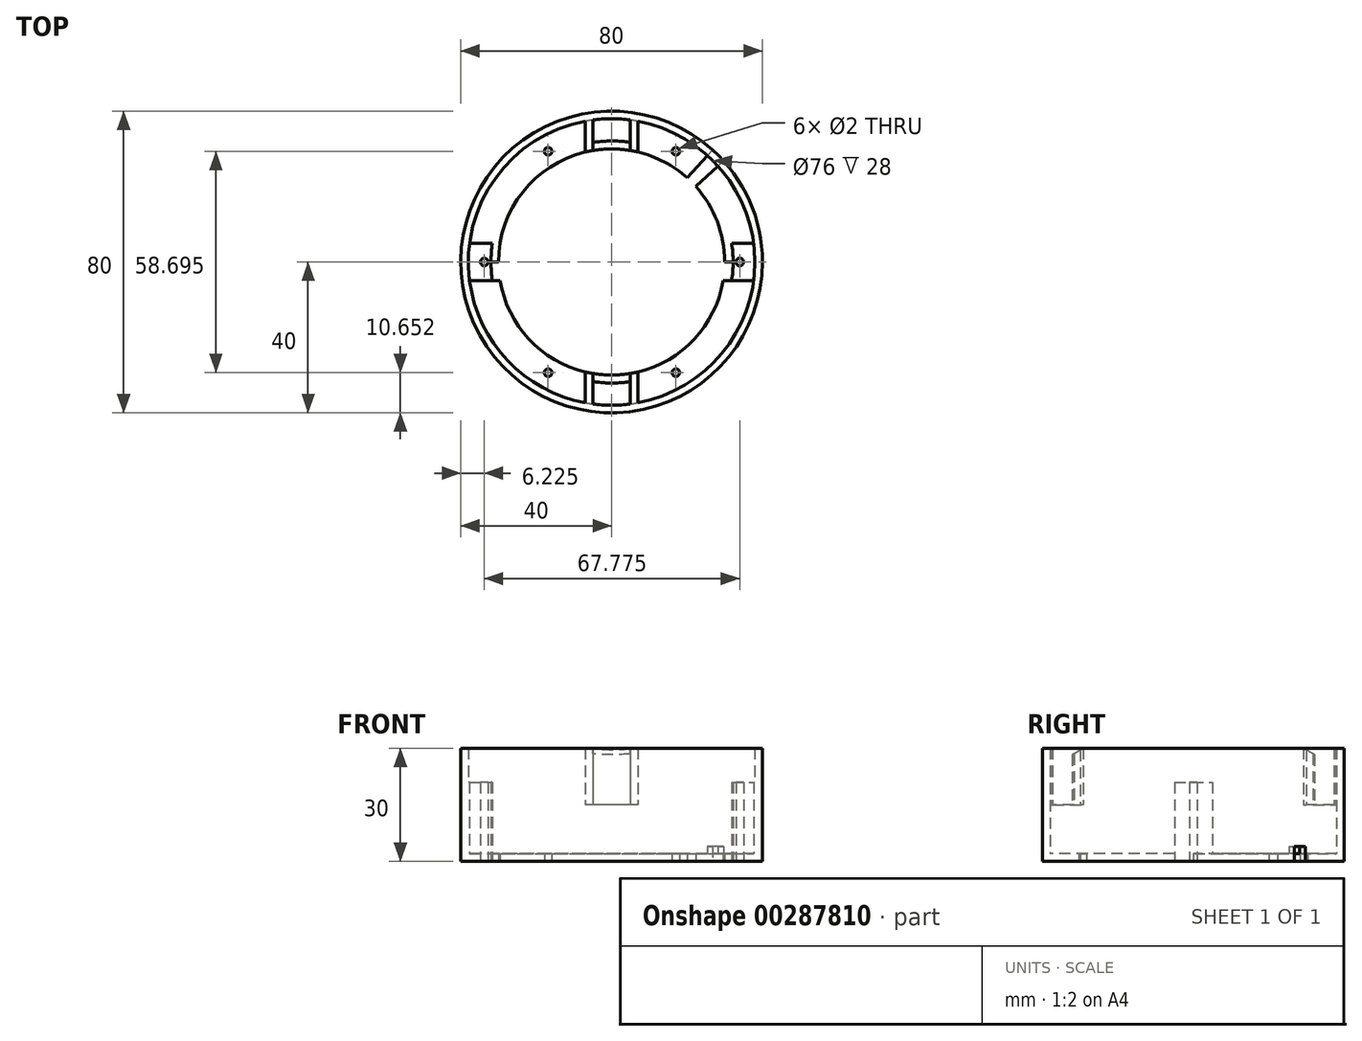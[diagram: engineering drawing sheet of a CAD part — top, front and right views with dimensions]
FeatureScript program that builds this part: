
annotation { "Feature Type Name" : "Feature", "Feature Type Description" : "" }
export const myFeature = defineFeature(function(context is Context, id is Id, definition is map)
    precondition{}
    {
        {
            var Q0;
            Q0=qCreatedBy(makeId("Top.planeOp"),FACE);
            var sketch = newSketch(context, id + "F0", { "sketchPlane" : qUnion([Q0])});
            skCircle(sketch, "E0", {"center": v(0, 0) * mm, "radius": 38 * mm});
            skCircle(sketch, "E1", {"center": v(0, 0) * mm, "radius": 40 * mm});
            skCircle(sketch, "E2", {"center": v(0, 0) * mm, "radius": 30 * mm});
            skLineSegment(sketch, "E3", {"start": v(-40, 0) * mm, "end": v(40, 0) * mm});
            skLineSegment(sketch, "E4", {"start": v(-39.69, 5) * mm, "end": v(39.69, 5) * mm});
            skLineSegment(sketch, "E5.MirrorCS", {"start": v(-39.69, -5) * mm, "end": v(39.69, -5) * mm});
            skCircle(sketch, "E6", {"center": v(34, 0) * mm, "radius": 1 * mm});
            skLineSegment(sketch, "E7", {"start": v(0, 40) * mm, "end": v(0, -40) * mm});
            skCircle(sketch, "E8.1.0", {"center": v(17.06, -29.35) * mm, "radius": 1 * mm});
            skCircle(sketch, "E8.2.0", {"center": v(-16.83, -29.35) * mm, "radius": 1 * mm});
            skCircle(sketch, "E8.3.0", {"center": v(-33.78, 0) * mm, "radius": 1 * mm});
            skCircle(sketch, "E8.4.0", {"center": v(-16.83, 29.35) * mm, "radius": 1 * mm});
            skCircle(sketch, "E8.5.0", {"center": v(17.06, 29.35) * mm, "radius": 1 * mm});
            skPoint(sketch, "E8.center", {"position": v(0.11, 0) * mm});
            skLineSegment(sketch, "E8.anchor1", {"start": v(0.11, 0) * mm, "end": v(34, 0) * mm, "construction": true});
            skLineSegment(sketch, "E8.anchor2", {"start": v(0.11, 0) * mm, "end": v(17.06, 29.35) * mm, "construction": true});
            skLineSegment(sketch, "E9", {"start": v(5, 29.58) * mm, "end": v(5, 37.67) * mm});
            skLineSegment(sketch, "E10", {"start": v(7, 37.35) * mm, "end": v(7, 29.17) * mm});
            skLineSegment(sketch, "E11.MirrorCS", {"start": v(-7, 37.35) * mm, "end": v(-7, 29.17) * mm});
            skLineSegment(sketch, "E12.MirrorCS", {"start": v(-5, 29.58) * mm, "end": v(-5, 37.67) * mm});
            skLineSegment(sketch, "E13.MirrorCS", {"start": v(-7, -37.35) * mm, "end": v(-7, -29.17) * mm});
            skLineSegment(sketch, "E14.MirrorCS", {"start": v(-5, -29.58) * mm, "end": v(-5, -37.67) * mm});
            skLineSegment(sketch, "E15.MirrorCS", {"start": v(5, -29.58) * mm, "end": v(5, -37.67) * mm});
            skLineSegment(sketch, "E16.MirrorCS", {"start": v(7, -37.35) * mm, "end": v(7, -29.17) * mm});
            skCircle(sketch, "E17", {"center": v(0.11, 0) * mm, "radius": 32.11 * mm});
            skLineSegment(sketch, "E18", {"start": v(0, 0) * mm, "end": v(28.28, 28.28) * mm});
            skLineSegment(sketch, "E19", {"start": v(0, 0) * mm, "end": v(29.73, 26.77) * mm});
            skLineSegment(sketch, "E20.MirrorCS", {"start": v(0, 0) * mm, "end": v(26.77, 29.73) * mm});
            skLineSegment(sketch, "E21", {"start": v(-12, 36.06) * mm, "end": v(-12, 27.5) * mm});
            skLineSegment(sketch, "E22.MirrorCS", {"start": v(12, 36.06) * mm, "end": v(12, 27.5) * mm});
            skLineSegment(sketch, "E23.MirrorCS", {"start": v(-12, -36.06) * mm, "end": v(-12, -27.5) * mm});
            skLineSegment(sketch, "E24.MirrorCS", {"start": v(12, -36.06) * mm, "end": v(12, -27.5) * mm});
            skSolve(sketch);
        }
        {
            var Q0;
            {var subQ0=sQuery(id+"F0.wireOp",EDGE,"E7");var subQ1=sQuery(id+"F0.wireOp",EDGE,"E0");var subQ2=makeQuery(id+"F0.imprint","INTERSECT",VERTEX,{"disambiguationData":[OD(0.0)],"derivedFrom":[subQ1,subQ0]});Q0=makeQuery(id+"F0.imprint","IMPRINT",FACE,{"disambiguationData":[TD([[makeQuery(id+"F0.imprint","IMPRINT",EDGE,{"disambiguationData":[TD([[subQ2,-1.0]])],"derivedFrom":subQ1}),-1.0]])]});}
            var Q1;
            {var subQ0=sQuery(id+"F0.wireOp",EDGE,"E4");var subQ1=sQuery(id+"F0.wireOp",EDGE,"E0");var subQ2=makeQuery(id+"F0.imprint","INTERSECT",VERTEX,{"disambiguationData":[OD(1.0)],"derivedFrom":[subQ1,subQ0]});Q1=makeQuery(id+"F0.imprint","IMPRINT",FACE,{"disambiguationData":[TD([[makeQuery(id+"F0.imprint","IMPRINT",EDGE,{"disambiguationData":[TD([[subQ2,-1.0]])],"derivedFrom":subQ1}),-1.0]])]});}
            var Q2;
            {var subQ0=sQuery(id+"F0.wireOp",EDGE,"E3");var subQ1=sQuery(id+"F0.wireOp",EDGE,"E0");var subQ2=makeQuery(id+"F0.imprint","INTERSECT",VERTEX,{"disambiguationData":[OD(1.0)],"derivedFrom":[subQ1,subQ0]});Q2=makeQuery(id+"F0.imprint","IMPRINT",FACE,{"disambiguationData":[TD([[makeQuery(id+"F0.imprint","IMPRINT",EDGE,{"disambiguationData":[TD([[subQ2,-1.0]])],"derivedFrom":subQ1}),-1.0]])]});}
            var Q3;
            {var subQ0=sQuery(id+"F0.wireOp",EDGE,"E5.MirrorCS");var subQ1=sQuery(id+"F0.wireOp",EDGE,"E0");var subQ2=makeQuery(id+"F0.imprint","INTERSECT",VERTEX,{"disambiguationData":[OD(0.0)],"derivedFrom":[subQ1,subQ0]});Q3=makeQuery(id+"F0.imprint","IMPRINT",FACE,{"disambiguationData":[TD([[makeQuery(id+"F0.imprint","IMPRINT",EDGE,{"disambiguationData":[TD([[subQ2,-1.0]])],"derivedFrom":subQ1}),-1.0]])]});}
            var Q4;
            {var subQ0=sQuery(id+"F0.wireOp",EDGE,"E7");var subQ1=sQuery(id+"F0.wireOp",EDGE,"E0");var subQ2=makeQuery(id+"F0.imprint","INTERSECT",VERTEX,{"disambiguationData":[OD(1.0)],"derivedFrom":[subQ1,subQ0]});Q4=makeQuery(id+"F0.imprint","IMPRINT",FACE,{"disambiguationData":[TD([[makeQuery(id+"F0.imprint","IMPRINT",EDGE,{"disambiguationData":[TD([[subQ2,-1.0]])],"derivedFrom":subQ1}),-1.0]])]});}
            var Q5;
            {var subQ0=sQuery(id+"F0.wireOp",EDGE,"E3");var subQ1=sQuery(id+"F0.wireOp",EDGE,"E0");var subQ2=makeQuery(id+"F0.imprint","INTERSECT",VERTEX,{"disambiguationData":[OD(0.0)],"derivedFrom":[subQ1,subQ0]});Q5=makeQuery(id+"F0.imprint","IMPRINT",FACE,{"disambiguationData":[TD([[makeQuery(id+"F0.imprint","IMPRINT",EDGE,{"disambiguationData":[TD([[subQ2,1.0]])],"derivedFrom":subQ1}),-1.0]])]});}
            var Q6;
            {var subQ0=sQuery(id+"F0.wireOp",EDGE,"E4");var subQ1=sQuery(id+"F0.wireOp",EDGE,"E0");var subQ2=makeQuery(id+"F0.imprint","INTERSECT",VERTEX,{"disambiguationData":[OD(0.0)],"derivedFrom":[subQ1,subQ0]});Q6=makeQuery(id+"F0.imprint","IMPRINT",FACE,{"disambiguationData":[TD([[makeQuery(id+"F0.imprint","IMPRINT",EDGE,{"disambiguationData":[TD([[subQ2,1.0]])],"derivedFrom":subQ1}),-1.0]])]});}
            var Q7;
            {var subQ0=sQuery(id+"F0.wireOp",EDGE,"E4");var subQ1=sQuery(id+"F0.wireOp",EDGE,"E0");var subQ2=makeQuery(id+"F0.imprint","INTERSECT",VERTEX,{"disambiguationData":[OD(0.0)],"derivedFrom":[subQ1,subQ0]});Q7=makeQuery(id+"F0.imprint","IMPRINT",FACE,{"disambiguationData":[TD([[makeQuery(id+"F0.imprint","IMPRINT",EDGE,{"disambiguationData":[TD([[subQ2,-1.0]])],"derivedFrom":subQ1}),-1.0]])]});}
            var Q8;
            {var subQ5=sQuery(id+"F0.wireOp",EDGE,"E0");var subQ8=makeQuery(id+"F0.imprint","INTERSECT",VERTEX,{"derivedFrom":[subQ5,sQuery(id+"F0.wireOp",EDGE,"E10")]});Q8=makeQuery(id+"F0.imprint","IMPRINT",FACE,{"disambiguationData":[TD([[makeQuery(id+"F0.imprint","IMPRINT",EDGE,{"disambiguationData":[TD([[subQ8,1.0]])],"derivedFrom":subQ5}),-1.0]])]});}
            extrude(context, id + "F1", {"entities" : qUnion([Q0, Q1, Q2, Q3, Q4, Q5, Q6, Q7, Q8]), "depth" : 30 * mm});
        }
        {
            var Q0;
            {var subQ5=sQuery(id+"F0.wireOp",EDGE,"E0");var subQ8=sQuery(id+"F0.wireOp",EDGE,"E4");var subQ10=makeQuery(id+"F0.imprint","INTERSECT",VERTEX,{"disambiguationData":[OD(1.0)],"derivedFrom":[subQ5,subQ8]});Q0=makeQuery(id+"F0.imprint","IMPRINT",FACE,{"disambiguationData":[TD([[makeQuery(id+"F0.imprint","IMPRINT",EDGE,{"disambiguationData":[TD([[subQ10,-1.0]])],"derivedFrom":subQ5}),1.0]])]});}
            var Q1;
            {var subQ0=sQuery(id+"F0.wireOp",EDGE,"E3");var subQ8=sQuery(id+"F0.wireOp",EDGE,"E0");var subQ9=makeQuery(id+"F0.imprint","INTERSECT",VERTEX,{"disambiguationData":[OD(1.0)],"derivedFrom":[subQ8,subQ0]});Q1=makeQuery(id+"F0.imprint","IMPRINT",FACE,{"disambiguationData":[TD([[makeQuery(id+"F0.imprint","IMPRINT",EDGE,{"disambiguationData":[TD([[subQ9,-1.0]])],"derivedFrom":subQ8}),1.0]])]});}
            var Q2;
            {var subQ5=sQuery(id+"F0.wireOp",EDGE,"E0");var subQ8=sQuery(id+"F0.wireOp",EDGE,"E4");var subQ10=makeQuery(id+"F0.imprint","INTERSECT",VERTEX,{"disambiguationData":[OD(0.0)],"derivedFrom":[subQ5,subQ8]});Q2=makeQuery(id+"F0.imprint","IMPRINT",FACE,{"disambiguationData":[TD([[makeQuery(id+"F0.imprint","IMPRINT",EDGE,{"disambiguationData":[TD([[subQ10,1.0]])],"derivedFrom":subQ5}),1.0]])]});}
            var Q3;
            {var subQ0=sQuery(id+"F0.wireOp",EDGE,"E3");var subQ5=sQuery(id+"F0.wireOp",EDGE,"E0");var subQ6=makeQuery(id+"F0.imprint","INTERSECT",VERTEX,{"disambiguationData":[OD(0.0)],"derivedFrom":[subQ5,subQ0]});Q3=makeQuery(id+"F0.imprint","IMPRINT",FACE,{"disambiguationData":[TD([[makeQuery(id+"F0.imprint","IMPRINT",EDGE,{"disambiguationData":[TD([[subQ6,1.0]])],"derivedFrom":subQ5}),1.0]])]});}
            extrude(context, id + "F2", {"entities" : qUnion([Q0, Q1, Q2, Q3]), "operationType" : NewBodyOperationType.ADD, "depth" : 21 * mm});
        }
        {
            var Q0;
            {var subQ0=sQuery(id+"F0.wireOp",EDGE,"E11.MirrorCS");Q0=makeQuery(id+"F0.imprint","IMPRINT",FACE,{"disambiguationData":[TD([[makeQuery(id+"F0.imprint","IMPRINT",EDGE,{"derivedFrom":subQ0}),1.0]])]});}
            var Q1;
            {var subQ0=sQuery(id+"F0.wireOp",EDGE,"E9");Q1=makeQuery(id+"F0.imprint","IMPRINT",FACE,{"disambiguationData":[TD([[makeQuery(id+"F0.imprint","IMPRINT",EDGE,{"derivedFrom":subQ0}),-1.0]])]});}
            var Q2;
            {var subQ0=sQuery(id+"F0.wireOp",EDGE,"E15.MirrorCS");Q2=makeQuery(id+"F0.imprint","IMPRINT",FACE,{"disambiguationData":[TD([[makeQuery(id+"F0.imprint","IMPRINT",EDGE,{"derivedFrom":subQ0}),1.0]])]});}
            var Q3;
            {var subQ0=sQuery(id+"F0.wireOp",EDGE,"E13.MirrorCS");Q3=makeQuery(id+"F0.imprint","IMPRINT",FACE,{"disambiguationData":[TD([[makeQuery(id+"F0.imprint","IMPRINT",EDGE,{"derivedFrom":subQ0}),-1.0]])]});}
            extrude(context, id + "F3", {"entities" : qUnion([Q0, Q1, Q2, Q3]), "operationType" : NewBodyOperationType.ADD, "depth" : 30 * mm, "hasSecondDirection" : true, "secondDirectionOppositeDirection" : false, "secondDirectionDepth" : 15 * mm});
        }
        {
            var Q0;
            Q0=makeQuery(id+"F0.imprint","IMPRINT",FACE,{"disambiguationData":[TD([[makeQuery(id+"F0.imprint","IMPRINT",EDGE,{"derivedFrom":sQuery(id+"F0.wireOp",EDGE,"E8.4.0")}),-1.0]])]});
            var Q1;
            {var subQ0=sQuery(id+"F0.wireOp",EDGE,"E12.MirrorCS");Q1=makeQuery(id+"F0.imprint","IMPRINT",FACE,{"disambiguationData":[TD([[makeQuery(id+"F0.imprint","IMPRINT",EDGE,{"derivedFrom":subQ0}),-1.0]])]});}
            var Q2;
            {var subQ0=sQuery(id+"F0.wireOp",EDGE,"E9");Q2=makeQuery(id+"F0.imprint","IMPRINT",FACE,{"disambiguationData":[TD([[makeQuery(id+"F0.imprint","IMPRINT",EDGE,{"derivedFrom":subQ0}),1.0]])]});}
            var Q3;
            Q3=makeQuery(id+"F0.imprint","IMPRINT",FACE,{"disambiguationData":[TD([[makeQuery(id+"F0.imprint","IMPRINT",EDGE,{"derivedFrom":sQuery(id+"F0.wireOp",EDGE,"E8.5.0")}),-1.0]])]});
            var Q4;
            Q4=makeQuery(id+"F0.imprint","IMPRINT",FACE,{"disambiguationData":[TD([[makeQuery(id+"F0.imprint","IMPRINT",EDGE,{"derivedFrom":sQuery(id+"F0.wireOp",EDGE,"E8.1.0")}),-1.0]])]});
            var Q5;
            {var subQ0=sQuery(id+"F0.wireOp",EDGE,"E15.MirrorCS");Q5=makeQuery(id+"F0.imprint","IMPRINT",FACE,{"disambiguationData":[TD([[makeQuery(id+"F0.imprint","IMPRINT",EDGE,{"derivedFrom":subQ0}),-1.0]])]});}
            var Q6;
            {var subQ0=sQuery(id+"F0.wireOp",EDGE,"E14.MirrorCS");Q6=makeQuery(id+"F0.imprint","IMPRINT",FACE,{"disambiguationData":[TD([[makeQuery(id+"F0.imprint","IMPRINT",EDGE,{"derivedFrom":subQ0}),1.0]])]});}
            var Q7;
            Q7=makeQuery(id+"F0.imprint","IMPRINT",FACE,{"disambiguationData":[TD([[makeQuery(id+"F0.imprint","IMPRINT",EDGE,{"derivedFrom":sQuery(id+"F0.wireOp",EDGE,"E8.2.0")}),-1.0]])]});
            var Q8;
            {var subQ0=sQuery(id+"F0.wireOp",EDGE,"E11.MirrorCS");var subQ1=sQuery(id+"F0.wireOp",EDGE,"E2");var subQ2=makeQuery(id+"F0.imprint","INTERSECT",VERTEX,{"derivedFrom":[subQ1,subQ0]});Q8=makeQuery(id+"F0.imprint","IMPRINT",FACE,{"disambiguationData":[TD([[makeQuery(id+"F0.imprint","IMPRINT",EDGE,{"disambiguationData":[TD([[subQ2,-1.0]])],"derivedFrom":subQ1}),-1.0]])]});}
            var Q9;
            {var subQ0=sQuery(id+"F0.wireOp",EDGE,"E10");var subQ1=sQuery(id+"F0.wireOp",EDGE,"E2");var subQ2=makeQuery(id+"F0.imprint","INTERSECT",VERTEX,{"derivedFrom":[subQ1,subQ0]});Q9=makeQuery(id+"F0.imprint","IMPRINT",FACE,{"disambiguationData":[TD([[makeQuery(id+"F0.imprint","IMPRINT",EDGE,{"disambiguationData":[TD([[subQ2,1.0]])],"derivedFrom":subQ1}),-1.0]])]});}
            var Q10;
            {var subQ0=sQuery(id+"F0.wireOp",EDGE,"E16.MirrorCS");var subQ1=sQuery(id+"F0.wireOp",EDGE,"E2");var subQ2=makeQuery(id+"F0.imprint","INTERSECT",VERTEX,{"derivedFrom":[subQ1,subQ0]});Q10=makeQuery(id+"F0.imprint","IMPRINT",FACE,{"disambiguationData":[TD([[makeQuery(id+"F0.imprint","IMPRINT",EDGE,{"disambiguationData":[TD([[subQ2,-1.0]])],"derivedFrom":subQ1}),-1.0]])]});}
            var Q11;
            {var subQ0=sQuery(id+"F0.wireOp",EDGE,"E13.MirrorCS");var subQ1=sQuery(id+"F0.wireOp",EDGE,"E2");var subQ2=makeQuery(id+"F0.imprint","INTERSECT",VERTEX,{"derivedFrom":[subQ1,subQ0]});Q11=makeQuery(id+"F0.imprint","IMPRINT",FACE,{"disambiguationData":[TD([[makeQuery(id+"F0.imprint","IMPRINT",EDGE,{"disambiguationData":[TD([[subQ2,1.0]])],"derivedFrom":subQ1}),-1.0]])]});}
            var Q12;
            {var subQ0=sQuery(id+"F0.wireOp",EDGE,"E4");var subQ1=sQuery(id+"F0.wireOp",EDGE,"E2");var subQ2=makeQuery(id+"F0.imprint","INTERSECT",VERTEX,{"disambiguationData":[OD(1.0)],"derivedFrom":[subQ1,subQ0]});Q12=makeQuery(id+"F0.imprint","IMPRINT",FACE,{"disambiguationData":[TD([[makeQuery(id+"F0.imprint","IMPRINT",EDGE,{"disambiguationData":[TD([[subQ2,-1.0]])],"derivedFrom":subQ1}),-1.0]])]});}
            var Q13;
            {var subQ0=sQuery(id+"F0.wireOp",EDGE,"E3");var subQ1=sQuery(id+"F0.wireOp",EDGE,"E2");var subQ2=makeQuery(id+"F0.imprint","INTERSECT",VERTEX,{"disambiguationData":[OD(1.0)],"derivedFrom":[subQ1,subQ0]});Q13=makeQuery(id+"F0.imprint","IMPRINT",FACE,{"disambiguationData":[TD([[makeQuery(id+"F0.imprint","IMPRINT",EDGE,{"disambiguationData":[TD([[subQ2,-1.0]])],"derivedFrom":subQ1}),-1.0]])]});}
            var Q14;
            {var subQ0=sQuery(id+"F0.wireOp",EDGE,"E4");var subQ1=sQuery(id+"F0.wireOp",EDGE,"E2");var subQ2=makeQuery(id+"F0.imprint","INTERSECT",VERTEX,{"disambiguationData":[OD(0.0)],"derivedFrom":[subQ1,subQ0]});Q14=makeQuery(id+"F0.imprint","IMPRINT",FACE,{"disambiguationData":[TD([[makeQuery(id+"F0.imprint","IMPRINT",EDGE,{"disambiguationData":[TD([[subQ2,1.0]])],"derivedFrom":subQ1}),-1.0]])]});}
            var Q15;
            {var subQ0=sQuery(id+"F0.wireOp",EDGE,"E3");var subQ1=sQuery(id+"F0.wireOp",EDGE,"E2");var subQ2=makeQuery(id+"F0.imprint","INTERSECT",VERTEX,{"disambiguationData":[OD(0.0)],"derivedFrom":[subQ1,subQ0]});Q15=makeQuery(id+"F0.imprint","IMPRINT",FACE,{"disambiguationData":[TD([[makeQuery(id+"F0.imprint","IMPRINT",EDGE,{"disambiguationData":[TD([[subQ2,1.0]])],"derivedFrom":subQ1}),-1.0]])]});}
            var Q16;
            {var subQ0=sQuery(id+"F0.wireOp",EDGE,"E4");var subQ1=sQuery(id+"F0.wireOp",EDGE,"E0");var subQ2=makeQuery(id+"F0.imprint","INTERSECT",VERTEX,{"disambiguationData":[OD(0.0)],"derivedFrom":[subQ1,subQ0]});Q16=makeQuery(id+"F0.imprint","IMPRINT",FACE,{"disambiguationData":[TD([[makeQuery(id+"F0.imprint","IMPRINT",EDGE,{"disambiguationData":[TD([[subQ2,-1.0]])],"derivedFrom":subQ1}),1.0]])]});}
            var Q17;
            {var subQ0=sQuery(id+"F0.wireOp",EDGE,"E4");var subQ1=sQuery(id+"F0.wireOp",EDGE,"E2");var subQ2=makeQuery(id+"F0.imprint","INTERSECT",VERTEX,{"disambiguationData":[OD(0.0)],"derivedFrom":[subQ1,subQ0]});Q17=makeQuery(id+"F0.imprint","IMPRINT",FACE,{"disambiguationData":[TD([[makeQuery(id+"F0.imprint","IMPRINT",EDGE,{"disambiguationData":[TD([[subQ2,-1.0]])],"derivedFrom":subQ1}),-1.0]])]});}
            var Q18;
            {var subQ0=sQuery(id+"F0.wireOp",EDGE,"E13.MirrorCS");var subQ1=sQuery(id+"F0.wireOp",EDGE,"E2");var subQ2=makeQuery(id+"F0.imprint","INTERSECT",VERTEX,{"derivedFrom":[subQ1,subQ0]});Q18=makeQuery(id+"F0.imprint","IMPRINT",FACE,{"disambiguationData":[TD([[makeQuery(id+"F0.imprint","IMPRINT",EDGE,{"disambiguationData":[TD([[subQ2,-1.0]])],"derivedFrom":subQ1}),-1.0]])]});}
            var Q19;
            {var subQ0=sQuery(id+"F0.wireOp",EDGE,"E15.MirrorCS");var subQ1=sQuery(id+"F0.wireOp",EDGE,"E2");var subQ2=makeQuery(id+"F0.imprint","INTERSECT",VERTEX,{"derivedFrom":[subQ1,subQ0]});Q19=makeQuery(id+"F0.imprint","IMPRINT",FACE,{"disambiguationData":[TD([[makeQuery(id+"F0.imprint","IMPRINT",EDGE,{"disambiguationData":[TD([[subQ2,-1.0]])],"derivedFrom":subQ1}),-1.0]])]});}
            var Q20;
            {var subQ0=sQuery(id+"F0.wireOp",EDGE,"E11.MirrorCS");var subQ1=sQuery(id+"F0.wireOp",EDGE,"E2");var subQ2=makeQuery(id+"F0.imprint","INTERSECT",VERTEX,{"derivedFrom":[subQ1,subQ0]});Q20=makeQuery(id+"F0.imprint","IMPRINT",FACE,{"disambiguationData":[TD([[makeQuery(id+"F0.imprint","IMPRINT",EDGE,{"disambiguationData":[TD([[subQ2,1.0]])],"derivedFrom":subQ1}),-1.0]])]});}
            var Q21;
            {var subQ0=sQuery(id+"F0.wireOp",EDGE,"E11.MirrorCS");var subQ1=sQuery(id+"F0.wireOp",EDGE,"E0");var subQ2=makeQuery(id+"F0.imprint","INTERSECT",VERTEX,{"derivedFrom":[subQ1,subQ0]});Q21=makeQuery(id+"F0.imprint","IMPRINT",FACE,{"disambiguationData":[TD([[makeQuery(id+"F0.imprint","IMPRINT",EDGE,{"disambiguationData":[TD([[subQ2,1.0]])],"derivedFrom":subQ1}),1.0]])]});}
            var Q22;
            {var subQ0=sQuery(id+"F0.wireOp",EDGE,"E9");var subQ1=sQuery(id+"F0.wireOp",EDGE,"E0");var subQ2=makeQuery(id+"F0.imprint","INTERSECT",VERTEX,{"derivedFrom":[subQ1,subQ0]});Q22=makeQuery(id+"F0.imprint","IMPRINT",FACE,{"disambiguationData":[TD([[makeQuery(id+"F0.imprint","IMPRINT",EDGE,{"disambiguationData":[TD([[subQ2,1.0]])],"derivedFrom":subQ1}),1.0]])]});}
            var Q23;
            {var subQ0=sQuery(id+"F0.wireOp",EDGE,"E9");var subQ1=sQuery(id+"F0.wireOp",EDGE,"E2");var subQ2=makeQuery(id+"F0.imprint","INTERSECT",VERTEX,{"derivedFrom":[subQ1,subQ0]});Q23=makeQuery(id+"F0.imprint","IMPRINT",FACE,{"disambiguationData":[TD([[makeQuery(id+"F0.imprint","IMPRINT",EDGE,{"disambiguationData":[TD([[subQ2,1.0]])],"derivedFrom":subQ1}),-1.0]])]});}
            var Q24;
            {var subQ0=sQuery(id+"F0.wireOp",EDGE,"E13.MirrorCS");var subQ1=sQuery(id+"F0.wireOp",EDGE,"E0");var subQ2=makeQuery(id+"F0.imprint","INTERSECT",VERTEX,{"derivedFrom":[subQ1,subQ0]});Q24=makeQuery(id+"F0.imprint","IMPRINT",FACE,{"disambiguationData":[TD([[makeQuery(id+"F0.imprint","IMPRINT",EDGE,{"disambiguationData":[TD([[subQ2,-1.0]])],"derivedFrom":subQ1}),1.0]])]});}
            var Q25;
            {var subQ0=sQuery(id+"F0.wireOp",EDGE,"E15.MirrorCS");var subQ1=sQuery(id+"F0.wireOp",EDGE,"E0");var subQ2=makeQuery(id+"F0.imprint","INTERSECT",VERTEX,{"derivedFrom":[subQ1,subQ0]});Q25=makeQuery(id+"F0.imprint","IMPRINT",FACE,{"disambiguationData":[TD([[makeQuery(id+"F0.imprint","IMPRINT",EDGE,{"disambiguationData":[TD([[subQ2,-1.0]])],"derivedFrom":subQ1}),1.0]])]});}
            var Q26;
            {var subQ0=sQuery(id+"F0.wireOp",EDGE,"E10");var subQ1=sQuery(id+"F0.wireOp",EDGE,"E0");var subQ2=makeQuery(id+"F0.imprint","INTERSECT",VERTEX,{"derivedFrom":[subQ1,subQ0]});Q26=makeQuery(id+"F0.imprint","IMPRINT",FACE,{"disambiguationData":[TD([[makeQuery(id+"F0.imprint","IMPRINT",EDGE,{"disambiguationData":[TD([[subQ2,1.0]])],"derivedFrom":subQ1}),1.0]])]});}
            var Q27;
            {var subQ0=sQuery(id+"F0.wireOp",EDGE,"E11.MirrorCS");var subQ1=sQuery(id+"F0.wireOp",EDGE,"E0");var subQ2=makeQuery(id+"F0.imprint","INTERSECT",VERTEX,{"derivedFrom":[subQ1,subQ0]});Q27=makeQuery(id+"F0.imprint","IMPRINT",FACE,{"disambiguationData":[TD([[makeQuery(id+"F0.imprint","IMPRINT",EDGE,{"disambiguationData":[TD([[subQ2,-1.0]])],"derivedFrom":subQ1}),1.0]])]});}
            var Q28;
            {var subQ0=sQuery(id+"F0.wireOp",EDGE,"E21");var subQ1=sQuery(id+"F0.wireOp",EDGE,"E2");var subQ2=makeQuery(id+"F0.imprint","INTERSECT",VERTEX,{"derivedFrom":[subQ1,subQ0]});Q28=makeQuery(id+"F0.imprint","IMPRINT",FACE,{"disambiguationData":[TD([[makeQuery(id+"F0.imprint","IMPRINT",EDGE,{"disambiguationData":[TD([[subQ2,-1.0]])],"derivedFrom":subQ1}),-1.0]])]});}
            var Q29;
            {var subQ0=sQuery(id+"F0.wireOp",EDGE,"E22.MirrorCS");var subQ1=sQuery(id+"F0.wireOp",EDGE,"E2");var subQ2=makeQuery(id+"F0.imprint","INTERSECT",VERTEX,{"derivedFrom":[subQ1,subQ0]});Q29=makeQuery(id+"F0.imprint","IMPRINT",FACE,{"disambiguationData":[TD([[makeQuery(id+"F0.imprint","IMPRINT",EDGE,{"disambiguationData":[TD([[subQ2,1.0]])],"derivedFrom":subQ1}),-1.0]])]});}
            var Q30;
            {var subQ0=sQuery(id+"F0.wireOp",EDGE,"E24.MirrorCS");var subQ1=sQuery(id+"F0.wireOp",EDGE,"E2");var subQ2=makeQuery(id+"F0.imprint","INTERSECT",VERTEX,{"derivedFrom":[subQ1,subQ0]});Q30=makeQuery(id+"F0.imprint","IMPRINT",FACE,{"disambiguationData":[TD([[makeQuery(id+"F0.imprint","IMPRINT",EDGE,{"disambiguationData":[TD([[subQ2,-1.0]])],"derivedFrom":subQ1}),-1.0]])]});}
            var Q31;
            {var subQ0=sQuery(id+"F0.wireOp",EDGE,"E16.MirrorCS");var subQ1=sQuery(id+"F0.wireOp",EDGE,"E0");var subQ2=makeQuery(id+"F0.imprint","INTERSECT",VERTEX,{"derivedFrom":[subQ1,subQ0]});Q31=makeQuery(id+"F0.imprint","IMPRINT",FACE,{"disambiguationData":[TD([[makeQuery(id+"F0.imprint","IMPRINT",EDGE,{"disambiguationData":[TD([[subQ2,-1.0]])],"derivedFrom":subQ1}),1.0]])]});}
            var Q32;
            {var subQ0=sQuery(id+"F0.wireOp",EDGE,"E23.MirrorCS");var subQ1=sQuery(id+"F0.wireOp",EDGE,"E2");var subQ2=makeQuery(id+"F0.imprint","INTERSECT",VERTEX,{"derivedFrom":[subQ1,subQ0]});Q32=makeQuery(id+"F0.imprint","IMPRINT",FACE,{"disambiguationData":[TD([[makeQuery(id+"F0.imprint","IMPRINT",EDGE,{"disambiguationData":[TD([[subQ2,1.0]])],"derivedFrom":subQ1}),-1.0]])]});}
            var Q33;
            {var subQ0=sQuery(id+"F0.wireOp",EDGE,"E13.MirrorCS");var subQ1=sQuery(id+"F0.wireOp",EDGE,"E0");var subQ2=makeQuery(id+"F0.imprint","INTERSECT",VERTEX,{"derivedFrom":[subQ1,subQ0]});Q33=makeQuery(id+"F0.imprint","IMPRINT",FACE,{"disambiguationData":[TD([[makeQuery(id+"F0.imprint","IMPRINT",EDGE,{"disambiguationData":[TD([[subQ2,1.0]])],"derivedFrom":subQ1}),1.0]])]});}
            extrude(context, id + "F4", {"entities" : qUnion([Q0, Q1, Q2, Q3, Q4, Q5, Q6, Q7, Q8, Q9, Q10, Q11, Q12, Q13, Q14, Q15, Q16, Q17, Q18, Q19, Q20, Q21, Q22, Q23, Q24, Q25, Q26, Q27, Q28, Q29, Q30, Q31, Q32, Q33]), "operationType" : NewBodyOperationType.ADD, "depth" : 2 * mm});
        }
        {
            var Q0;
            {var subQ0=sQuery(id+"F0.wireOp",EDGE,"E9");var subQ1=sQuery(id+"F0.wireOp",EDGE,"E2");var subQ2=makeQuery(id+"F0.imprint","INTERSECT",VERTEX,{"derivedFrom":[subQ1,subQ0]});Q0=makeQuery(id+"F0.imprint","IMPRINT",FACE,{"disambiguationData":[TD([[makeQuery(id+"F0.imprint","IMPRINT",EDGE,{"disambiguationData":[TD([[subQ2,-1.0]])],"derivedFrom":subQ1}),-1.0]])]});}
            var Q1;
            {var subQ0=sQuery(id+"F0.wireOp",EDGE,"E12.MirrorCS");var subQ1=sQuery(id+"F0.wireOp",EDGE,"E2");var subQ2=makeQuery(id+"F0.imprint","INTERSECT",VERTEX,{"derivedFrom":[subQ1,subQ0]});Q1=makeQuery(id+"F0.imprint","IMPRINT",FACE,{"disambiguationData":[TD([[makeQuery(id+"F0.imprint","IMPRINT",EDGE,{"disambiguationData":[TD([[subQ2,1.0]])],"derivedFrom":subQ1}),-1.0]])]});}
            var Q2;
            {var subQ0=sQuery(id+"F0.wireOp",EDGE,"E15.MirrorCS");var subQ1=sQuery(id+"F0.wireOp",EDGE,"E2");var subQ2=makeQuery(id+"F0.imprint","INTERSECT",VERTEX,{"derivedFrom":[subQ1,subQ0]});Q2=makeQuery(id+"F0.imprint","IMPRINT",FACE,{"disambiguationData":[TD([[makeQuery(id+"F0.imprint","IMPRINT",EDGE,{"disambiguationData":[TD([[subQ2,1.0]])],"derivedFrom":subQ1}),-1.0]])]});}
            var Q3;
            {var subQ0=sQuery(id+"F0.wireOp",EDGE,"E14.MirrorCS");var subQ1=sQuery(id+"F0.wireOp",EDGE,"E2");var subQ2=makeQuery(id+"F0.imprint","INTERSECT",VERTEX,{"derivedFrom":[subQ1,subQ0]});Q3=makeQuery(id+"F0.imprint","IMPRINT",FACE,{"disambiguationData":[TD([[makeQuery(id+"F0.imprint","IMPRINT",EDGE,{"disambiguationData":[TD([[subQ2,-1.0]])],"derivedFrom":subQ1}),-1.0]])]});}
            extrude(context, id + "F5", {"entities" : qUnion([Q0, Q1, Q2, Q3]), "operationType" : NewBodyOperationType.ADD, "depth" : 30 * mm, "hasSecondDirection" : true, "secondDirectionOppositeDirection" : false, "secondDirectionDepth" : 15 * mm});
        }
        {
            var Q0;
            {var subQ0=sQuery(id+"F0.wireOp",EDGE,"E18");var subQ1=sQuery(id+"F0.wireOp",EDGE,"E0");var subQ2=makeQuery(id+"F0.imprint","INTERSECT",VERTEX,{"derivedFrom":[subQ1,subQ0]});Q0=makeQuery(id+"F0.imprint","IMPRINT",FACE,{"disambiguationData":[TD([[makeQuery(id+"F0.imprint","IMPRINT",EDGE,{"disambiguationData":[TD([[subQ2,-1.0]])],"derivedFrom":subQ1}),-1.0]])]});}
            var Q1;
            {var subQ0=sQuery(id+"F0.wireOp",EDGE,"E19");var subQ1=sQuery(id+"F0.wireOp",EDGE,"E0");var subQ2=makeQuery(id+"F0.imprint","INTERSECT",VERTEX,{"derivedFrom":[subQ1,subQ0]});Q1=makeQuery(id+"F0.imprint","IMPRINT",FACE,{"disambiguationData":[TD([[makeQuery(id+"F0.imprint","IMPRINT",EDGE,{"disambiguationData":[TD([[subQ2,-1.0]])],"derivedFrom":subQ1}),-1.0]])]});}
            extrude(context, id + "F6", {"entities" : qUnion([Q0, Q1]), "operationType" : NewBodyOperationType.ADD, "depth" : 30 * mm, "hasSecondDirection" : true, "secondDirectionOppositeDirection" : false, "secondDirectionDepth" : 4 * mm});
        }
        {
            var Q0;
            Q0=makeQuery(id+"F3.opExtrude","SWEPT_FACE",FACE,{"disambiguationData":[OSD([sQuery(id+"F0.wireOp",EDGE,"E10")])]});
            var sketch = newSketch(context, id + "F7", { "sketchPlane" : qUnion([Q0])});
            skLineSegment(sketch, "E25", {"start": v(29.17, 30) * mm, "end": v(32.17, 30) * mm});
            skLineSegment(sketch, "E26", {"start": v(32.17, 30) * mm, "end": v(32.17, 28.27) * mm});
            skLineSegment(sketch, "E27", {"start": v(32.17, 28.27) * mm, "end": v(29.17, 30) * mm});
            skLineSegment(sketch, "E28.MirrorCS", {"start": v(-29.17, 30) * mm, "end": v(-32.17, 30) * mm});
            skLineSegment(sketch, "E29.MirrorCS", {"start": v(-32.17, 28.27) * mm, "end": v(-29.17, 30) * mm});
            skLineSegment(sketch, "E30.MirrorCS", {"start": v(-32.17, 30) * mm, "end": v(-32.17, 28.27) * mm});
            skSolve(sketch);
        }
        {
            var Q0;
            Q0=makeQuery(id+"F7.imprint","IMPRINT",FACE,{"disambiguationData":[TD([[makeQuery(id+"F7.imprint","IMPRINT",EDGE,{"derivedFrom":sQuery(id+"F7.wireOp",EDGE,"E25")}),1.0]])]});
            var Q1;
            Q1=makeQuery(id+"F7.imprint","IMPRINT",FACE,{"disambiguationData":[TD([[makeQuery(id+"F7.imprint","IMPRINT",EDGE,{"derivedFrom":sQuery(id+"F7.wireOp",EDGE,"E28.MirrorCS")}),1.0]])]});
            extrude(context, id + "F8", {"entities" : qUnion([Q0, Q1]), "operationType" : NewBodyOperationType.REMOVE, "oppositeDirection" : true, "depth" : 12 * mm, "hasSecondDirection" : true, "secondDirectionOppositeDirection" : true, "secondDirectionDepth" : 2 * mm});
        }
    });
